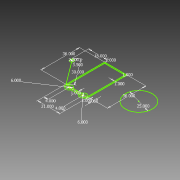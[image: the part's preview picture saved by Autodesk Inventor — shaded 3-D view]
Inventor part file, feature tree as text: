
AUTODESK INVENTOR PART (.ipt)
format: ipt  version: 2014 SP1 (Build 180222100, 222)  size: 81,408 bytes
history: native  units: in
note: dims shown in document units (in); Inventor stores cm internally (conversion verified against a paired STEP export)
features: sketch x1
ambient origin geometry x8: Origin, YZ Plane, XZ Plane, XY Plane, X Axis, Y Axis, Z Axis, Center Point
feature tree (1):
  sketch  "Sketch1"  dims[d3=21.0in d4=2.0in d5=6.0in d6=6.0in d7=4.0in d8=4.0in d9=1.0in d11=36.0in d12=36.0in d14=25.0in d16=1.0in d21=30.0in d23=3.5in d25=1.0in d26=1.0in d27=1.0in d28=18.0in d29=2.5in]
